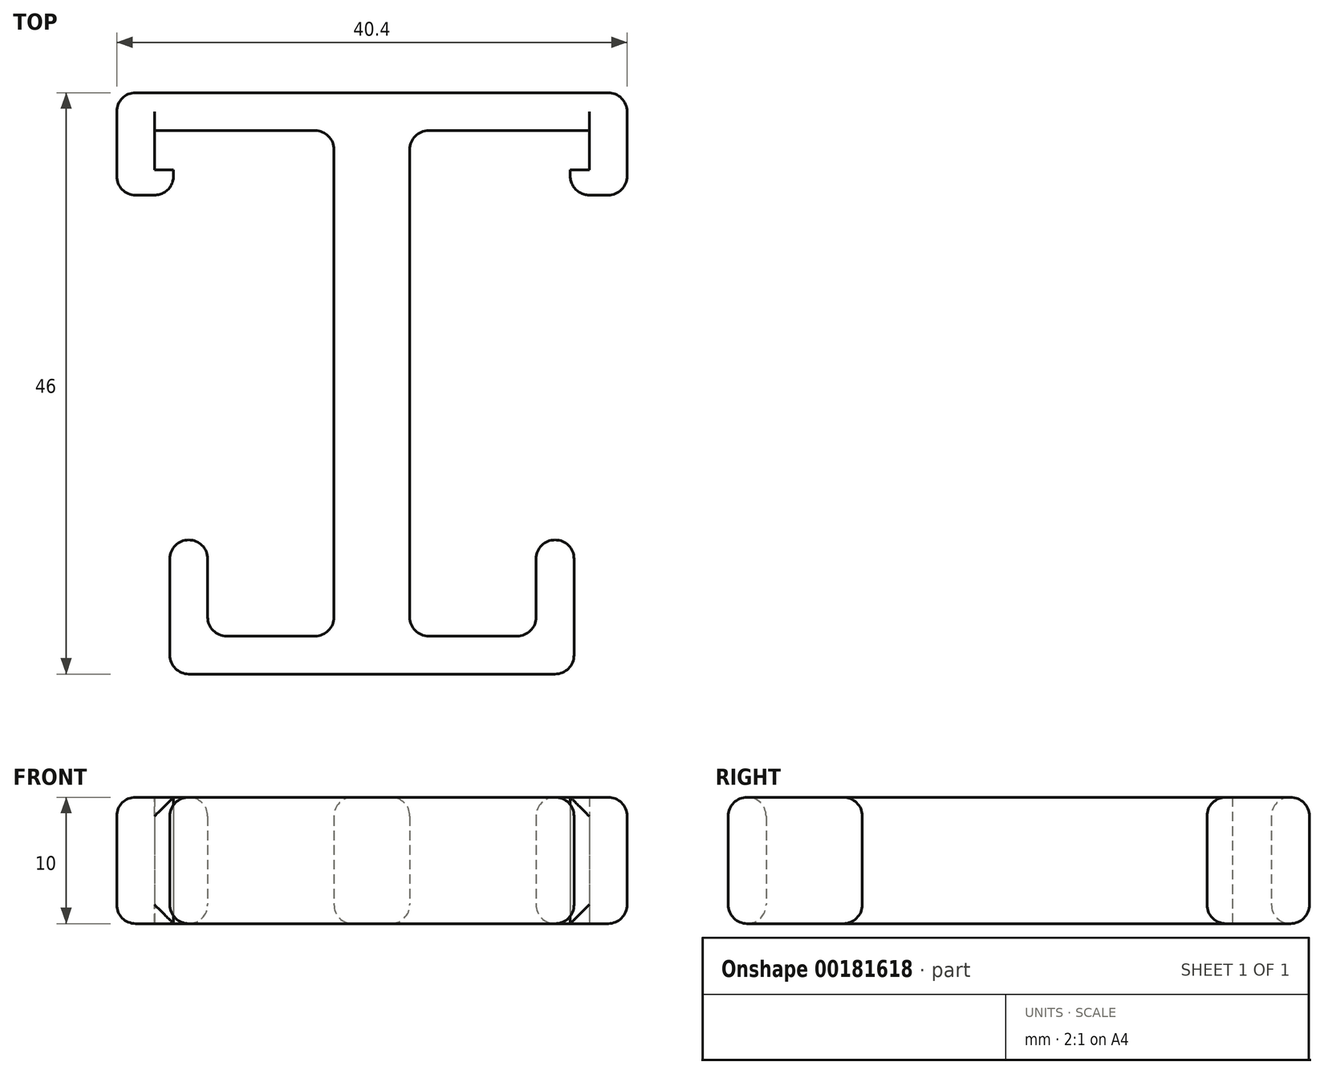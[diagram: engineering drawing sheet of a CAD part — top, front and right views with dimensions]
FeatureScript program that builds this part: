
annotation { "Feature Type Name" : "Feature", "Feature Type Description" : "" }
export const myFeature = defineFeature(function(context is Context, id is Id, definition is map)
    precondition{}
    {
        {
            var Q0;
            Q0=qCreatedBy(makeId("Top.planeOp"),FACE);
            var sketch = newSketch(context, id + "F0", { "sketchPlane" : qUnion([Q0])});
            skLineSegment(sketch, "E0", {"start": v(-17.2, 4.92) * mm, "end": v(-17.2, 8.02) * mm});
            skLineSegment(sketch, "E1", {"start": v(-17.2, 8.02) * mm, "end": v(-3, 8.02) * mm});
            skLineSegment(sketch, "E2", {"start": v(-3, 8.02) * mm, "end": v(-3, -31.98) * mm});
            skLineSegment(sketch, "E3", {"start": v(-3, -31.98) * mm, "end": v(-13, -31.98) * mm});
            skLineSegment(sketch, "E4", {"start": v(-13, -31.98) * mm, "end": v(-13, -24.37) * mm});
            skLineSegment(sketch, "E5", {"start": v(-13, -24.37) * mm, "end": v(-16, -24.37) * mm});
            skLineSegment(sketch, "E6", {"start": v(-16, -24.37) * mm, "end": v(-16, -34.98) * mm});
            skLineSegment(sketch, "E7", {"start": v(-16, -34.98) * mm, "end": v(0, -34.98) * mm});
            skLineSegment(sketch, "E8", {"start": v(0, -34.98) * mm, "end": v(0, 11.02) * mm});
            skLineSegment(sketch, "E9", {"start": v(0, 11.02) * mm, "end": v(-20.2, 11.02) * mm});
            skLineSegment(sketch, "E10", {"start": v(-17.2, 4.92) * mm, "end": v(-15.7, 4.92) * mm});
            skLineSegment(sketch, "E11", {"start": v(-15.7, 4.92) * mm, "end": v(-15.7, 2.92) * mm});
            skLineSegment(sketch, "E12", {"start": v(-15.7, 2.92) * mm, "end": v(-20.2, 2.92) * mm});
            skLineSegment(sketch, "E13", {"start": v(-20.2, 11.02) * mm, "end": v(-20.2, 2.92) * mm});
            skSolve(sketch);
        }
        {
            var Q0;
            Q0=makeQuery(id+"F0.imprint","IMPRINT",FACE,{"disambiguationData":[TD([[makeQuery(id+"F0.imprint","IMPRINT",EDGE,{"derivedFrom":sQuery(id+"F0.wireOp",EDGE,"E0")}),1.0]])]});
            extrude(context, id + "F1", {"entities" : qUnion([Q0]), "depth" : 10 * mm});
        }
        {
            var Q0;
            Q0=makeQuery(id+"F1.opExtrude","SWEPT_BODY",BODY,{"disambiguationData":[OSD([sQuery(id+"F0.wireOp",EDGE,"E0"),sQuery(id+"F0.wireOp",EDGE,"E1"),sQuery(id+"F0.wireOp",EDGE,"E2"),sQuery(id+"F0.wireOp",EDGE,"E3"),sQuery(id+"F0.wireOp",EDGE,"E4"),sQuery(id+"F0.wireOp",EDGE,"E5"),sQuery(id+"F0.wireOp",EDGE,"E6"),sQuery(id+"F0.wireOp",EDGE,"E7"),sQuery(id+"F0.wireOp",EDGE,"E8"),sQuery(id+"F0.wireOp",EDGE,"E9"),sQuery(id+"F0.wireOp",EDGE,"yGI4GcSN-I9eH-aRO7-dwlI-FHjQqPXa0aMT"),sQuery(id+"F0.wireOp",EDGE,"SnjWdeeQ-tDTH-36kn-Kiin-wOcu2xQtzhWk")])]});
            var Q1;
            Q1=makeQuery(id+"F1.opExtrude","SWEPT_FACE",FACE,{"disambiguationData":[OSD([sQuery(id+"F0.wireOp",EDGE,"E8")])]});
            mirror(context, id + "F2", {"operationType" : NewBodyOperationType.ADD, "entities" : qUnion([Q0]), "mirrorPlane" : qUnion([Q1])});
        }
        {
            var Q0;
            Q0=makeQuery(id+"F1.opExtrude","SWEPT_EDGE",EDGE,{"disambiguationData":[OSD([sQuery(id+"F0.wireOp",EDGE,"E2"),sQuery(id+"F0.wireOp",EDGE,"E3")])]});
            var Q1;
            Q1=makeQuery(id+"F1.opExtrude","SWEPT_EDGE",EDGE,{"disambiguationData":[OSD([sQuery(id+"F0.wireOp",EDGE,"E3"),sQuery(id+"F0.wireOp",EDGE,"E4")])]});
            var Q2;
            Q2=makeQuery(id+"F2.opPattern","COPY",EDGE,{"derivedFrom":makeQuery(id+"F1.opExtrude","SWEPT_EDGE",EDGE,{"disambiguationData":[OSD([sQuery(id+"F0.wireOp",EDGE,"E3"),sQuery(id+"F0.wireOp",EDGE,"E4")])]}),"instanceName":"1"});
            var Q3;
            Q3=makeQuery(id+"F2.opPattern","COPY",EDGE,{"derivedFrom":makeQuery(id+"F1.opExtrude","SWEPT_EDGE",EDGE,{"disambiguationData":[OSD([sQuery(id+"F0.wireOp",EDGE,"E2"),sQuery(id+"F0.wireOp",EDGE,"E3")])]}),"instanceName":"1"});
            var Q4;
            Q4=makeQuery(id+"F2.opPattern","COPY",EDGE,{"derivedFrom":makeQuery(id+"F1.opExtrude","SWEPT_EDGE",EDGE,{"disambiguationData":[OSD([sQuery(id+"F0.wireOp",EDGE,"E6"),sQuery(id+"F0.wireOp",EDGE,"E7")])]}),"instanceName":"1"});
            var Q5;
            Q5=makeQuery(id+"F1.opExtrude","SWEPT_EDGE",EDGE,{"disambiguationData":[OSD([sQuery(id+"F0.wireOp",EDGE,"E6"),sQuery(id+"F0.wireOp",EDGE,"E7")])]});
            var Q6;
            Q6=makeQuery(id+"F1.opExtrude","SWEPT_EDGE",EDGE,{"disambiguationData":[OSD([sQuery(id+"F0.wireOp",EDGE,"E9"),sQuery(id+"F0.wireOp",EDGE,"yGI4GcSN-I9eH-aRO7-dwlI-FHjQqPXa0aMT")])]});
            var Q7;
            Q7=makeQuery(id+"F2.opPattern","COPY",EDGE,{"derivedFrom":makeQuery(id+"F1.opExtrude","SWEPT_EDGE",EDGE,{"disambiguationData":[OSD([sQuery(id+"F0.wireOp",EDGE,"E9"),sQuery(id+"F0.wireOp",EDGE,"yGI4GcSN-I9eH-aRO7-dwlI-FHjQqPXa0aMT")])]}),"instanceName":"1"});
            var Q8;
            {var subQ0=makeQuery(id+"F1.opExtrude","CAP_EDGE",EDGE,{"disambiguationData":[OSD([sQuery(id+"F0.wireOp",EDGE,"E9")])],"isStart":false});Q8=makeQuery(id+"F2.boolean.opBoolean","MERGE",EDGE,{"derivedFrom":[subQ0,makeQuery(id+"F2.opPattern","COPY",EDGE,{"derivedFrom":subQ0,"instanceName":"1"})]});}
            var Q9;
            {var subQ0=makeQuery(id+"F1.opExtrude","CAP_EDGE",EDGE,{"disambiguationData":[OSD([sQuery(id+"F0.wireOp",EDGE,"E9")])],"isStart":true});Q9=makeQuery(id+"F2.boolean.opBoolean","MERGE",EDGE,{"derivedFrom":[subQ0,makeQuery(id+"F2.opPattern","COPY",EDGE,{"derivedFrom":subQ0,"instanceName":"1"})]});}
            var Q10;
            {var subQ0=makeQuery(id+"F1.opExtrude","CAP_EDGE",EDGE,{"disambiguationData":[OSD([sQuery(id+"F0.wireOp",EDGE,"E7")])],"isStart":false});Q10=makeQuery(id+"F2.boolean.opBoolean","MERGE",EDGE,{"derivedFrom":[subQ0,makeQuery(id+"F2.opPattern","COPY",EDGE,{"derivedFrom":subQ0,"instanceName":"1"})]});}
            var Q11;
            {var subQ0=makeQuery(id+"F1.opExtrude","CAP_EDGE",EDGE,{"disambiguationData":[OSD([sQuery(id+"F0.wireOp",EDGE,"E7")])],"isStart":true});Q11=makeQuery(id+"F2.boolean.opBoolean","MERGE",EDGE,{"derivedFrom":[subQ0,makeQuery(id+"F2.opPattern","COPY",EDGE,{"derivedFrom":subQ0,"instanceName":"1"})]});}
            var Q12;
            Q12=makeQuery(id+"F2.opPattern","COPY",EDGE,{"derivedFrom":makeQuery(id+"F1.opExtrude","CAP_EDGE",EDGE,{"disambiguationData":[OSD([sQuery(id+"F0.wireOp",EDGE,"E2")])],"isStart":false}),"instanceName":"1"});
            var Q13;
            Q13=makeQuery(id+"F1.opExtrude","CAP_EDGE",EDGE,{"disambiguationData":[OSD([sQuery(id+"F0.wireOp",EDGE,"E2")])],"isStart":false});
            var Q14;
            Q14=makeQuery(id+"F2.opPattern","COPY",EDGE,{"derivedFrom":makeQuery(id+"F1.opExtrude","CAP_EDGE",EDGE,{"disambiguationData":[OSD([sQuery(id+"F0.wireOp",EDGE,"E2")])],"isStart":true}),"instanceName":"1"});
            var Q15;
            Q15=makeQuery(id+"F1.opExtrude","CAP_EDGE",EDGE,{"disambiguationData":[OSD([sQuery(id+"F0.wireOp",EDGE,"E2")])],"isStart":true});
            var Q16;
            Q16=makeQuery(id+"F1.opExtrude","CAP_EDGE",EDGE,{"disambiguationData":[OSD([sQuery(id+"F0.wireOp",EDGE,"E6")])],"isStart":false});
            var Q17;
            Q17=makeQuery(id+"F1.opExtrude","SWEPT_EDGE",EDGE,{"disambiguationData":[OSD([sQuery(id+"F0.wireOp",EDGE,"E5"),sQuery(id+"F0.wireOp",EDGE,"E6")])]});
            var Q18;
            Q18=makeQuery(id+"F1.opExtrude","CAP_EDGE",EDGE,{"disambiguationData":[OSD([sQuery(id+"F0.wireOp",EDGE,"E4")])],"isStart":true});
            var Q19;
            Q19=makeQuery(id+"F2.opPattern","COPY",EDGE,{"derivedFrom":makeQuery(id+"F1.opExtrude","SWEPT_EDGE",EDGE,{"disambiguationData":[OSD([sQuery(id+"F0.wireOp",EDGE,"E4"),sQuery(id+"F0.wireOp",EDGE,"E5")])]}),"instanceName":"1"});
            var Q20;
            Q20=makeQuery(id+"F2.opPattern","COPY",EDGE,{"derivedFrom":makeQuery(id+"F1.opExtrude","CAP_EDGE",EDGE,{"disambiguationData":[OSD([sQuery(id+"F0.wireOp",EDGE,"E6")])],"isStart":true}),"instanceName":"1"});
            var Q21;
            Q21=makeQuery(id+"F2.opPattern","COPY",EDGE,{"derivedFrom":makeQuery(id+"F1.opExtrude","CAP_EDGE",EDGE,{"disambiguationData":[OSD([sQuery(id+"F0.wireOp",EDGE,"E6")])],"isStart":false}),"instanceName":"1"});
            var Q22;
            Q22=makeQuery(id+"F1.opExtrude","SWEPT_FACE",FACE,{"disambiguationData":[OSD([sQuery(id+"F0.wireOp",EDGE,"E4")])]});
            var Q23;
            Q23=makeQuery(id+"F2.opPattern","COPY",EDGE,{"derivedFrom":makeQuery(id+"F1.opExtrude","CAP_EDGE",EDGE,{"disambiguationData":[OSD([sQuery(id+"F0.wireOp",EDGE,"E4")])],"isStart":true}),"instanceName":"1"});
            var Q24;
            Q24=makeQuery(id+"F2.opPattern","COPY",EDGE,{"derivedFrom":makeQuery(id+"F1.opExtrude","CAP_EDGE",EDGE,{"disambiguationData":[OSD([sQuery(id+"F0.wireOp",EDGE,"E4")])],"isStart":false}),"instanceName":"1"});
            var Q25;
            Q25=makeQuery(id+"F2.opPattern","COPY",EDGE,{"derivedFrom":makeQuery(id+"F1.opExtrude","SWEPT_EDGE",EDGE,{"disambiguationData":[OSD([sQuery(id+"F0.wireOp",EDGE,"E5"),sQuery(id+"F0.wireOp",EDGE,"E6")])]}),"instanceName":"1"});
            var Q26;
            Q26=makeQuery(id+"F1.opExtrude","CAP_EDGE",EDGE,{"disambiguationData":[OSD([sQuery(id+"F0.wireOp",EDGE,"E3")])],"isStart":false});
            var Q27;
            Q27=makeQuery(id+"F2.opPattern","COPY",EDGE,{"derivedFrom":makeQuery(id+"F1.opExtrude","CAP_EDGE",EDGE,{"disambiguationData":[OSD([sQuery(id+"F0.wireOp",EDGE,"E3")])],"isStart":false}),"instanceName":"1"});
            var Q28;
            Q28=makeQuery(id+"F1.opExtrude","CAP_EDGE",EDGE,{"disambiguationData":[OSD([sQuery(id+"F0.wireOp",EDGE,"E3")])],"isStart":true});
            var Q29;
            Q29=makeQuery(id+"F2.opPattern","COPY",EDGE,{"derivedFrom":makeQuery(id+"F1.opExtrude","CAP_EDGE",EDGE,{"disambiguationData":[OSD([sQuery(id+"F0.wireOp",EDGE,"E3")])],"isStart":true}),"instanceName":"1"});
            var Q30;
            Q30=makeQuery(id+"F1.opExtrude","CAP_EDGE",EDGE,{"disambiguationData":[OSD([sQuery(id+"F0.wireOp",EDGE,"E5")])],"isStart":false});
            var Q31;
            Q31=makeQuery(id+"F1.opExtrude","CAP_EDGE",EDGE,{"disambiguationData":[OSD([sQuery(id+"F0.wireOp",EDGE,"E5")])],"isStart":true});
            var Q32;
            Q32=makeQuery(id+"F2.opPattern","COPY",EDGE,{"derivedFrom":makeQuery(id+"F1.opExtrude","CAP_EDGE",EDGE,{"disambiguationData":[OSD([sQuery(id+"F0.wireOp",EDGE,"E5")])],"isStart":false}),"instanceName":"1"});
            var Q33;
            Q33=makeQuery(id+"F2.opPattern","COPY",EDGE,{"derivedFrom":makeQuery(id+"F1.opExtrude","CAP_EDGE",EDGE,{"disambiguationData":[OSD([sQuery(id+"F0.wireOp",EDGE,"E5")])],"isStart":true}),"instanceName":"1"});
            var Q34;
            Q34=makeQuery(id+"F1.opExtrude","CAP_EDGE",EDGE,{"disambiguationData":[OSD([sQuery(id+"F0.wireOp",EDGE,"E6")])],"isStart":true});
            var Q35;
            Q35=makeQuery(id+"F2.opPattern","COPY",EDGE,{"derivedFrom":makeQuery(id+"F1.opExtrude","CAP_EDGE",EDGE,{"disambiguationData":[OSD([sQuery(id+"F0.wireOp",EDGE,"yGI4GcSN-I9eH-aRO7-dwlI-FHjQqPXa0aMT")])],"isStart":true}),"instanceName":"1"});
            var Q36;
            Q36=makeQuery(id+"F1.opExtrude","CAP_EDGE",EDGE,{"disambiguationData":[OSD([sQuery(id+"F0.wireOp",EDGE,"yGI4GcSN-I9eH-aRO7-dwlI-FHjQqPXa0aMT")])],"isStart":true});
            var Q37;
            Q37=makeQuery(id+"F1.opExtrude","CAP_EDGE",EDGE,{"disambiguationData":[OSD([sQuery(id+"F0.wireOp",EDGE,"yGI4GcSN-I9eH-aRO7-dwlI-FHjQqPXa0aMT")])],"isStart":false});
            var Q38;
            Q38=makeQuery(id+"F2.opPattern","COPY",EDGE,{"derivedFrom":makeQuery(id+"F1.opExtrude","CAP_EDGE",EDGE,{"disambiguationData":[OSD([sQuery(id+"F0.wireOp",EDGE,"yGI4GcSN-I9eH-aRO7-dwlI-FHjQqPXa0aMT")])],"isStart":false}),"instanceName":"1"});
            var Q39;
            Q39=makeQuery(id+"F1.opExtrude","CAP_EDGE",EDGE,{"disambiguationData":[OSD([sQuery(id+"F0.wireOp",EDGE,"E13")])],"isStart":false});
            var Q40;
            Q40=makeQuery(id+"F1.opExtrude","CAP_EDGE",EDGE,{"disambiguationData":[OSD([sQuery(id+"F0.wireOp",EDGE,"E13")])],"isStart":true});
            var Q41;
            Q41=makeQuery(id+"F2.opPattern","COPY",EDGE,{"derivedFrom":makeQuery(id+"F1.opExtrude","CAP_EDGE",EDGE,{"disambiguationData":[OSD([sQuery(id+"F0.wireOp",EDGE,"E13")])],"isStart":false}),"instanceName":"1"});
            var Q42;
            Q42=makeQuery(id+"F2.opPattern","COPY",EDGE,{"derivedFrom":makeQuery(id+"F1.opExtrude","CAP_EDGE",EDGE,{"disambiguationData":[OSD([sQuery(id+"F0.wireOp",EDGE,"E13")])],"isStart":true}),"instanceName":"1"});
            var Q43;
            Q43=makeQuery(id+"F2.opPattern","COPY",EDGE,{"derivedFrom":makeQuery(id+"F1.opExtrude","SWEPT_EDGE",EDGE,{"disambiguationData":[OSD([sQuery(id+"F0.wireOp",EDGE,"E1"),sQuery(id+"F0.wireOp",EDGE,"E2")])]}),"instanceName":"1"});
            var Q44;
            Q44=makeQuery(id+"F1.opExtrude","SWEPT_EDGE",EDGE,{"disambiguationData":[OSD([sQuery(id+"F0.wireOp",EDGE,"E12"),sQuery(id+"F0.wireOp",EDGE,"E13")])]});
            var Q45;
            Q45=makeQuery(id+"F2.opPattern","COPY",EDGE,{"derivedFrom":makeQuery(id+"F1.opExtrude","SWEPT_EDGE",EDGE,{"disambiguationData":[OSD([sQuery(id+"F0.wireOp",EDGE,"E12"),sQuery(id+"F0.wireOp",EDGE,"E13")])]}),"instanceName":"1"});
            var Q46;
            Q46=makeQuery(id+"F1.opExtrude","SWEPT_EDGE",EDGE,{"disambiguationData":[OSD([sQuery(id+"F0.wireOp",EDGE,"E11"),sQuery(id+"F0.wireOp",EDGE,"E12")])]});
            var Q47;
            Q47=makeQuery(id+"F2.opPattern","COPY",EDGE,{"derivedFrom":makeQuery(id+"F1.opExtrude","SWEPT_EDGE",EDGE,{"disambiguationData":[OSD([sQuery(id+"F0.wireOp",EDGE,"E11"),sQuery(id+"F0.wireOp",EDGE,"E12")])]}),"instanceName":"1"});
            var Q48;
            Q48=makeQuery(id+"F1.opExtrude","CAP_EDGE",EDGE,{"disambiguationData":[OSD([sQuery(id+"F0.wireOp",EDGE,"E12")])],"isStart":false});
            var Q49;
            Q49=makeQuery(id+"F1.opExtrude","CAP_EDGE",EDGE,{"disambiguationData":[OSD([sQuery(id+"F0.wireOp",EDGE,"E12")])],"isStart":true});
            var Q50;
            Q50=makeQuery(id+"F2.opPattern","COPY",EDGE,{"derivedFrom":makeQuery(id+"F1.opExtrude","CAP_EDGE",EDGE,{"disambiguationData":[OSD([sQuery(id+"F0.wireOp",EDGE,"E12")])],"isStart":true}),"instanceName":"1"});
            var Q51;
            Q51=makeQuery(id+"F2.opPattern","COPY",EDGE,{"derivedFrom":makeQuery(id+"F1.opExtrude","CAP_EDGE",EDGE,{"disambiguationData":[OSD([sQuery(id+"F0.wireOp",EDGE,"E12")])],"isStart":false}),"instanceName":"1"});
            var Q52;
            Q52=makeQuery(id+"F1.opExtrude","CAP_EDGE",EDGE,{"disambiguationData":[OSD([sQuery(id+"F0.wireOp",EDGE,"E1")])],"isStart":false});
            var Q53;
            Q53=makeQuery(id+"F1.opExtrude","CAP_EDGE",EDGE,{"disambiguationData":[OSD([sQuery(id+"F0.wireOp",EDGE,"E1")])],"isStart":true});
            var Q54;
            Q54=makeQuery(id+"F2.opPattern","COPY",EDGE,{"derivedFrom":makeQuery(id+"F1.opExtrude","CAP_EDGE",EDGE,{"disambiguationData":[OSD([sQuery(id+"F0.wireOp",EDGE,"E1")])],"isStart":false}),"instanceName":"1"});
            var Q55;
            Q55=makeQuery(id+"F2.opPattern","COPY",EDGE,{"derivedFrom":makeQuery(id+"F1.opExtrude","CAP_EDGE",EDGE,{"disambiguationData":[OSD([sQuery(id+"F0.wireOp",EDGE,"E1")])],"isStart":true}),"instanceName":"1"});
            var Q56;
            Q56=makeQuery(id+"F1.opExtrude","SWEPT_EDGE",EDGE,{"disambiguationData":[OSD([sQuery(id+"F0.wireOp",EDGE,"E1"),sQuery(id+"F0.wireOp",EDGE,"E2")])]});
            fillet(context, id + "F3", {"entities" : qUnion([Q0, Q1, Q2, Q3, Q4, Q5, Q6, Q7, Q8, Q9, Q10, Q11, Q12, Q13, Q14, Q15, Q16, Q17, Q18, Q19, Q20, Q21, Q22, Q23, Q24, Q25, Q26, Q27, Q28, Q29, Q30, Q31, Q32, Q33, Q34, Q35, Q36, Q37, Q38, Q39, Q40, Q41, Q42, Q43, Q44, Q45, Q46, Q47, Q48, Q49, Q50, Q51, Q52, Q53, Q54, Q55, Q56]), "radius" : 1.5 * mm, "tangentPropagation" : true, "allowEdgeOverflow" : false});
        }
    });
